# Revit family: LAMP_MOODY G2 1700 + MINI ROUND FIXED REFLECTOR
name_source: partatom
category: Luminarias
revit_build: Autodesk Revit 2015 (Build: 20140606_1530(x64)
units: mm (PartAtom-declared; Revit-internal decimal feet)

## types (9) — shared parameters
Altura reflector = 53 mm
Black reflector code = MORFRD072FXB
Black reflector datasheet = http://www.lamp.es
Black reflector description = MOODY REF RD FX Ø72 BK.
Black reflector finish = Matt black
Black reflector model = MORFRD072FXB
Cambio de temperatura de color de luz atenuada = <Ninguno>
Comentarios de tipo = Availability of switching reflector colour when placed in a project.
Copper reflector code = MORFRD072FXC
Copper reflector datasheet = http://www.lamp.es
Copper reflector description = MOODY REF RD FX Ø72 CO.
Copper reflector finish = Metalized matt copper
Copper reflector model = MORFRD072FXC
Core datasheet = http://www.lamp.es
Core description = MOODY CORE 1200 VWW MFL
Core diameter = 50 mm  [stored 0.164042 ft]
Fabricante = LAMP
Filtro de color = 16777215
Gear = Electronic
IEE = A++
Installation instructions = https://www.lamp.es
Insulation class = II
LED Lifetime = 50.000 L70 B10
Last update = 28/08/2019
Luminaire type = Indoor - Recessed Downlight
Lámpara = COB LED
MacAdam = 3
Manufacturer URL = http://www.lamp.es
Manufacturer country = Spain
Manufacturer name = LAMP
Material Muelle Emp. = LAMP_Acero genérico
Material Reflector Blanco = LAMP_PC Reflector Moody BL
Material Reflector Cobre = LAMP_PC Reflector Moody CO
Material Reflector Negro = LAMP_PC Reflector Moody NG
Material Reflector Plata = LAMP_PC Reflector Moody GR
Model explanation = Availability of switching reflector colour when placed in a project.
Plum = 14 W
Power = 12 W
Power Supply = 220-240V 50/60Hz
Product URL = https://www.lamp.es
Protection rating = IP20
Recessed diameter = 68 mm
Reflector diameter = 72 mm  [stored 0.23622 ft]
Silver reflector code = MORFRD072FXM
Silver reflector datasheet = http://www.lamp.es
Silver reflector description = MOODY REF RD FX Ø72 MET.
Silver reflector finish = Metalized matt silver
Silver reflector model = MORFRD072FXM
Total height = 140 mm  [stored 0.459318 ft]
Total weight = 0.34 kg
Type = COB PHILIPS
White reflector code = MORFRD072FXW
White reflector datasheet = http://www.lamp.es
White reflector description = MOODY REF RD FX Ø72 WH.
White reflector finish = Matt white
White reflector model = MORFRD072FXW
Ángulo de inclinación = 90.00°

## per-type parameters (varying)
| type | Archivo de red fotométrica | CRI | Core model | Core product code | Descripción | Efficacy | UGR |
| 2700K FLOOD | MO215FL927TB+MORFRD072FXM.IES | 90 | MO215FL927TB | MO215FL927TB | MOODY G2 1700 VWW FL TRIAC BK. | 66 lm/W | 23 |
| 2700K SPOT | MO215SP927TB+MORFRD072FXM.IES | 90 | MO215SP927TB | MO215SP927TB | MOODY G2 1700 VWW SP TRIAC BK. | 66 lm/W | 23 |
| 2700K WIDE FLOOD | MO215WF927TB+MORFRD072FXM.IES | 90 | MO215WF927TB | MO215WF927TB | MOODY G2 1700 VWW WFL TRIAC BK. | 66 lm/W | 23 |
| 3000K FLOOD | MO215FL830TB+MORFRD072FXM.IES | 80 | MO215FL830TB | MO215FL830TB | MOODY G2 1700 WW FL TRIAC BK. | 81 lm/W | 23 |
| 3000K SPOT | MO215SP830TB+MORFRD072FXM.IES | 80 | MO215SP830TB | MO215SP830TB | MOODY G2 1700 WW SP TRIAC BK. | 81 lm/W | 23 |
| 3000K WIDE FLOOD | MO215WF830TB+MORFRD072FXM.IES | 80 | MO215WF830TB | MO215WF830TB | MOODY G2 1700 WW WFL TRIAC BK. | 81 lm/W | 23 |
| 4000K FLOOD | MO215FL840TB+MORFRD072FXM.IES | 80 | MO215FL840TB | MO215FL840TB | MOODY G2 1700 NW FL TRIAC BK. | 86 lm/W | 24 |
| 4000K SPOT | MO215SP840TB+MORFRD072FXM.IES | 80 | MO215SP840TB | MO215SP840TB | MOODY G2 1700 NW SP TRIAC BK. | 86 lm/W | 24 |
| 4000K WIDE FLOOD | MO215WF840TB+MORFRD072FXM.IES | 80 | MO215WF840TB | MO215WF840TB | MOODY G2 1700 NW WFL TRIAC BK. | 86 lm/W | 24 |

note: [stored X ft] marks values corroborated as IEEE doubles in the binary element streams (Revit-internal decimal feet)
